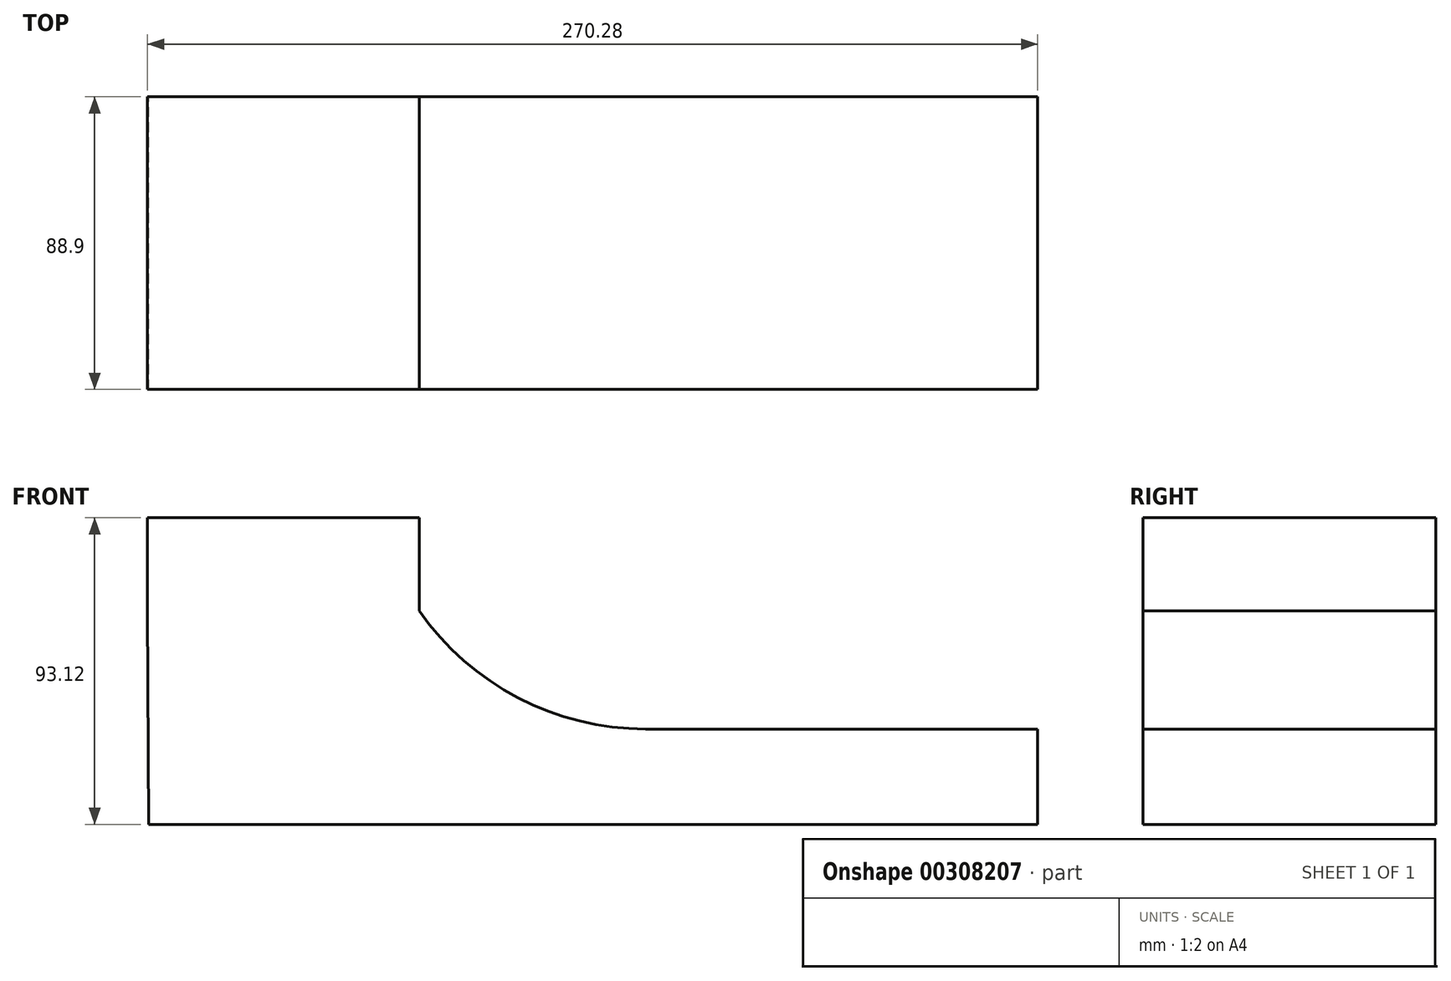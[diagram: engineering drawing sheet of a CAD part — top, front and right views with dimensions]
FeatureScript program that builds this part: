
annotation { "Feature Type Name" : "Feature", "Feature Type Description" : "" }
export const myFeature = defineFeature(function(context is Context, id is Id, definition is map)
    precondition{}
    {
        {
            var Q0;
            Q0=qCreatedBy(makeId("Front.planeOp"),FACE);
            var sketch = newSketch(context, id + "F0", { "sketchPlane" : qUnion([Q0])});
            skLineSegment(sketch, "E0.bottom", {"start": v(-59.52, 14.48) * mm, "end": v(59.52, 14.48) * mm});
            skLineSegment(sketch, "E0.top", {"start": v(-59.52, -14.48) * mm, "end": v(59.52, -14.48) * mm});
            skLineSegment(sketch, "E0.left", {"start": v(-59.52, 14.48) * mm, "end": v(-59.52, -14.48) * mm});
            skLineSegment(sketch, "E0.right", {"start": v(59.52, 14.48) * mm, "end": v(59.52, -14.48) * mm});
            skPoint(sketch, "E0.middle", {"position": v(0, 0) * mm});
            skLineSegment(sketch, "E1.bottom", {"start": v(-128.22, 78.64) * mm, "end": v(-210.76, 78.64) * mm});
            skLineSegment(sketch, "E1.top", {"start": v(-128.22, 50.31) * mm, "end": v(-210.76, 50.31) * mm});
            skLineSegment(sketch, "E1.left", {"start": v(-128.22, 78.64) * mm, "end": v(-128.22, 50.31) * mm});
            skLineSegment(sketch, "E1.right", {"start": v(-210.76, 78.64) * mm, "end": v(-210.76, 50.31) * mm});
            skPoint(sketch, "E1.middle", {"position": v(-169.5, 64.48) * mm});
            skArc(sketch, "E2", {"start": v(-59.52, 14.48) * mm, "mid": v(-98.26, 23.98) * mm, "end": v(-128.22, 50.31) * mm});
            skLineSegment(sketch, "E3", {"start": v(-59.52, -14.48) * mm, "end": v(-210.45, -14.48) * mm});
            skLineSegment(sketch, "E4", {"start": v(-210.45, -14.48) * mm, "end": v(-210.76, 50.31) * mm});
            skPoint(sketch, "E5.3.internal.snap0", {"position": v(-98.26, 23.98) * mm});
            skSolve(sketch);
        }
        {
            var Q0;
            Q0=makeQuery(id+"F0.imprint","IMPRINT",FACE,{"disambiguationData":[TD([[makeQuery(id+"F0.imprint","IMPRINT",EDGE,{"derivedFrom":sQuery(id+"F0.wireOp",EDGE,"E0.bottom")}),-1.0]])]});
            var Q1;
            Q1=makeQuery(id+"F0.imprint","IMPRINT",FACE,{"disambiguationData":[TD([[makeQuery(id+"F0.imprint","IMPRINT",EDGE,{"derivedFrom":sQuery(id+"F0.wireOp",EDGE,"E0.left")}),-1.0]])]});
            var Q2;
            Q2=makeQuery(id+"F0.imprint","IMPRINT",FACE,{"disambiguationData":[TD([[makeQuery(id+"F0.imprint","IMPRINT",EDGE,{"derivedFrom":sQuery(id+"F0.wireOp",EDGE,"E1.bottom")}),1.0]])]});
            extrude(context, id + "F1", {"entities" : qUnion([Q0, Q1, Q2]), "endBound" : BoundingType.SYMMETRIC, "depth" : 127 * mm});
        }
        {
            var Q0;
            Q0=makeQuery(id+"F1.opExtrude","CAP_FACE",FACE,{"disambiguationData":[OSD([sQuery(id+"F0.wireOp",EDGE,"E0.bottom"),sQuery(id+"F0.wireOp",EDGE,"E0.top"),sQuery(id+"F0.wireOp",EDGE,"E0.left"),sQuery(id+"F0.wireOp",EDGE,"E0.right")])],"isStart":true});
            var Q1;
            Q1=makeQuery(id+"F1.opExtrude","CAP_FACE",FACE,{"disambiguationData":[OSD([sQuery(id+"F0.wireOp",EDGE,"E0.bottom"),sQuery(id+"F0.wireOp",EDGE,"E0.top"),sQuery(id+"F0.wireOp",EDGE,"E0.left"),sQuery(id+"F0.wireOp",EDGE,"E0.right")])],"isStart":false});
            extrude(context, id + "F2", {"entities" : qUnion([Q0, Q1]), "operationType" : NewBodyOperationType.REMOVE, "oppositeDirection" : true, "depth" : 38.1 * mm});
        }
    });
